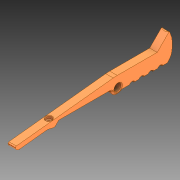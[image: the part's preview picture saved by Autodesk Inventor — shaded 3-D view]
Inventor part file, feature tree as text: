
AUTODESK INVENTOR PART (.ipt)
format: ipt  version: 2020 (Build 240168000, 168)  size: 202,240 bytes
history: native  units: in
note: dims shown in document units (in); Inventor stores cm internally (conversion verified against a paired STEP export)
features: extrude x1, fillet x1, sketch x1, imported_body x1
ambient origin geometry x8: Origin, YZ Plane, XZ Plane, XY Plane, X Axis, Y Axis, Z Axis, Center Point
bodies: Solid1 (feature_tree)
feature tree (4):
  extrude  "Extrusion1"  Depth=0.3937in TaperAngle=0.0deg
  fillet  "Fillet1"  Radius=0.1378in
  sketch  "Sketch1"  dims[d0=1.1811in d1=0.3937in d2=0.0in d3=0.1378in d4=0.0394in]
  imported_body  "Base1"
